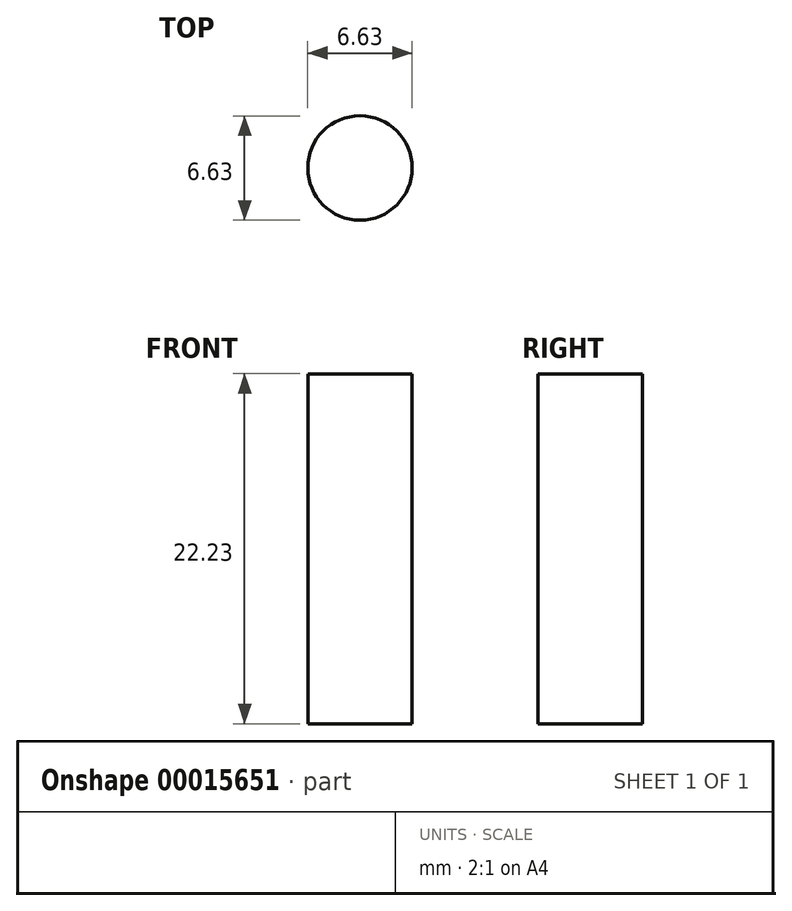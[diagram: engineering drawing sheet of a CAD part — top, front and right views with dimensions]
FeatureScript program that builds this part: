
annotation { "Feature Type Name" : "Feature", "Feature Type Description" : "" }
export const myFeature = defineFeature(function(context is Context, id is Id, definition is map)
    precondition{}
    {
        {
            var Q0;
            Q0=qCreatedBy(makeId("Top.planeOp"),FACE);
            var sketch = newSketch(context, id + "F0", { "sketchPlane" : qUnion([Q0])});
            skCircle(sketch, "E0", {"center": v(-62.75, 46.07) * mm, "radius": 3.31 * mm});
            skSolve(sketch);
        }
        {
            var Q0;
            Q0=sQuery(id+"F0.wireOp",EDGE,"E0");
            extrude(context, id + "F1", {"bodyType" : ToolBodyType.SURFACE, "surfaceEntities" : qUnion([Q0]), "depth" : 22.22 * mm});
        }
    });
